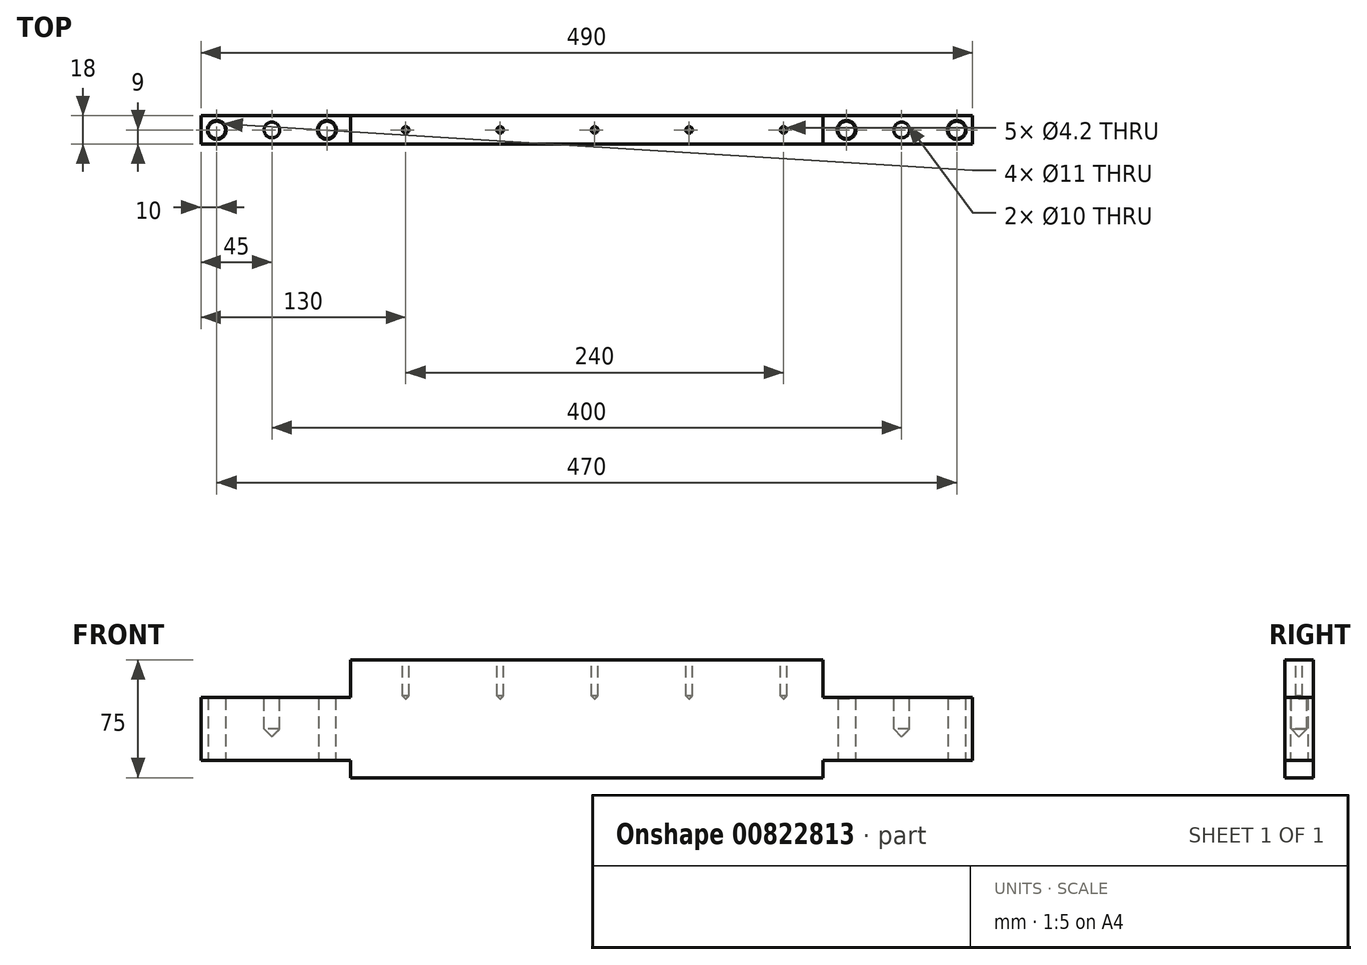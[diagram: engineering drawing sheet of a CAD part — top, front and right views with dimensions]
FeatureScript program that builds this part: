
annotation { "Feature Type Name" : "Feature", "Feature Type Description" : "" }
export const myFeature = defineFeature(function(context is Context, id is Id, definition is map)
    precondition{}
    {
        {
            var Q0;
            Q0=qCreatedBy(makeId("Front.planeOp"),FACE);
            var sketch = newSketch(context, id + "F0", { "sketchPlane" : qUnion([Q0])});
            skLineSegment(sketch, "E0.bottom", {"start": v(-245, -37.5) * mm, "end": v(245, -37.5) * mm});
            skLineSegment(sketch, "E0.top", {"start": v(-150, 37.5) * mm, "end": v(150, 37.5) * mm});
            skLineSegment(sketch, "E0.left", {"start": v(-245, -37.5) * mm, "end": v(-245, 13.5) * mm});
            skLineSegment(sketch, "E0.right", {"start": v(245, -37.5) * mm, "end": v(245, 13.5) * mm});
            skPoint(sketch, "E0.middle", {"position": v(0, 0) * mm});
            skLineSegment(sketch, "E1", {"start": v(-245, 13.5) * mm, "end": v(-150, 13.5) * mm});
            skLineSegment(sketch, "E2", {"start": v(-150, 13.5) * mm, "end": v(-150, 37.5) * mm});
            skLineSegment(sketch, "E3", {"start": v(0, 0) * mm, "end": v(0, 109.73) * mm, "construction": true});
            skPoint(sketch, "E3.endSnap0", {"position": v(0, 37.5) * mm});
            skLineSegment(sketch, "E4.MirrorCS", {"start": v(245, 13.5) * mm, "end": v(150, 13.5) * mm});
            skLineSegment(sketch, "E5.MirrorCS", {"start": v(150, 13.5) * mm, "end": v(150, 37.5) * mm});
            skPoint(sketch, "E6.orphan", {"position": v(-245, 37.5) * mm});
            skPoint(sketch, "E7.orphan", {"position": v(245, 37.5) * mm});
            skSolve(sketch);
        }
        {
            var Q0;
            Q0=qSketchRegion(id+"F0",true);
            extrude(context, id + "F1", {"entities" : qUnion([Q0]), "endBound" : BoundingType.SYMMETRIC, "depth" : 18 * mm, "offsetDistance" : 25 * mm});
        }
        {
            var Q0;
            Q0=makeQuery(id+"F1.opExtrude","SWEPT_FACE",FACE,{"disambiguationData":[OSD([sQuery(id+"F0.wireOp",EDGE,"E0.bottom")])]});
            var sketch = newSketch(context, id + "F2", { "sketchPlane" : qUnion([Q0])});
            skLineSegment(sketch, "E8", {"start": v(0, 0) * mm, "end": v(0, 32.03) * mm, "construction": true});
            skLineSegment(sketch, "E9", {"start": v(0, 32.03) * mm, "end": v(235, 0) * mm, "construction": true});
            skLineSegment(sketch, "E10", {"start": v(235, 0) * mm, "end": v(0, 0) * mm, "construction": true});
            skCircle(sketch, "E11", {"center": v(235, 0) * mm, "radius": 5.5 * mm});
            skCircle(sketch, "E12", {"center": v(165, 0) * mm, "radius": 5.5 * mm});
            skCircle(sketch, "E13.MirrorC", {"center": v(-165, 0) * mm, "radius": 5.5 * mm});
            skCircle(sketch, "E14.MirrorC", {"center": v(-235, 0) * mm, "radius": 5.5 * mm});
            skSolve(sketch);
        }
        {
            var Q0;
            Q0=qSketchRegion(id+"F2",true);
            extrude(context, id + "F3", {"entities" : qUnion([Q0]), "operationType" : NewBodyOperationType.REMOVE, "endBound" : BoundingType.UP_TO_NEXT, "oppositeDirection" : true, "depth" : 25 * mm, "offsetDistance" : 25 * mm});
        }
        {
            var Q0;
            Q0=makeQuery(id+"F1.opExtrude","SWEPT_FACE",FACE,{"disambiguationData":[OSD([sQuery(id+"F0.wireOp",EDGE,"E0.top")])]});
            var sketch = newSketch(context, id + "F4", { "sketchPlane" : qUnion([Q0])});
            skLineSegment(sketch, "E15", {"start": v(0, 0) * mm, "end": v(-175, 0) * mm, "construction": true});
            skLineSegment(sketch, "E16.0", {"start": v(-150, -9) * mm, "end": v(-150, 9) * mm, "construction": true});
            skCircle(sketch, "E17", {"center": v(-175, 0) * mm, "radius": 2.1 * mm, "construction": true});
            skLineSegment(sketch, "E18", {"start": v(-175, 0) * mm, "end": v(-195, 0) * mm, "construction": true});
            skCircle(sketch, "E19.1.0.0", {"center": v(-115, 0) * mm, "radius": 2.1 * mm});
            skCircle(sketch, "E19.2.0.0", {"center": v(-55, 0) * mm, "radius": 2.1 * mm});
            skCircle(sketch, "E19.3.0.0", {"center": v(5, 0) * mm, "radius": 2.1 * mm});
            skCircle(sketch, "E19.4.0.0", {"center": v(65, 0) * mm, "radius": 2.1 * mm});
            skCircle(sketch, "E19.5.0.0", {"center": v(125, 0) * mm, "radius": 2.1 * mm});
            skCircle(sketch, "E19.6.0.0", {"center": v(185, 0) * mm, "radius": 2.1 * mm, "construction": true});
            skCircle(sketch, "E19.7.0.0", {"center": v(245, 0) * mm, "radius": 2.1 * mm, "construction": true});
            skCircle(sketch, "E19.8.0.0", {"center": v(305, 0) * mm, "radius": 2.1 * mm, "construction": true});
            skLineSegment(sketch, "E19.direction1", {"start": v(-175, 0) * mm, "end": v(-115, 0) * mm, "construction": true});
            skLineSegment(sketch, "E20", {"start": v(0, 0) * mm, "end": v(0, 52.01) * mm, "construction": true});
            skLineSegment(sketch, "E21", {"start": v(0, 52.01) * mm, "end": v(-62, 56.3) * mm, "construction": true});
            skLineSegment(sketch, "E22", {"start": v(-62, 56.3) * mm, "end": v(-62, -65.3) * mm, "construction": true});
            skLineSegment(sketch, "E23.bottom", {"start": v(-24.5, 38.85) * mm, "end": v(-99.5, 38.85) * mm});
            skLineSegment(sketch, "E23.top", {"start": v(-24.5, -169.44) * mm, "end": v(-99.5, -169.44) * mm, "construction": true});
            skLineSegment(sketch, "E23.left", {"start": v(-24.5, 38.85) * mm, "end": v(-24.5, -169.44) * mm, "construction": true});
            skLineSegment(sketch, "E23.right", {"start": v(-99.5, 38.85) * mm, "end": v(-99.5, -169.44) * mm, "construction": true});
            skPoint(sketch, "E23.middle", {"position": v(-62, -65.3) * mm});
            skLineSegment(sketch, "E24.bottom", {"start": v(-112.5, 84.27) * mm, "end": v(-187.5, 84.27) * mm, "construction": true});
            skLineSegment(sketch, "E24.top", {"start": v(-112.5, -270.84) * mm, "end": v(-187.5, -270.84) * mm, "construction": true});
            skLineSegment(sketch, "E24.left", {"start": v(-112.5, 84.27) * mm, "end": v(-112.5, -270.84) * mm, "construction": true});
            skLineSegment(sketch, "E24.right", {"start": v(-187.5, 84.27) * mm, "end": v(-187.5, -270.84) * mm, "construction": true});
            skPoint(sketch, "E24.middle", {"position": v(-150, -93.28) * mm});
            skLineSegment(sketch, "E25", {"start": v(-150, -93.28) * mm, "end": v(0, -93.28) * mm, "construction": true});
            skLineSegment(sketch, "E26", {"start": v(0, -93.28) * mm, "end": v(0, 0) * mm, "construction": true});
            skSolve(sketch);
        }
        {
            var Q0;
            Q0=qSketchRegion(id+"F4",true);
            extrude(context, id + "F5", {"entities" : qUnion([Q0]), "operationType" : NewBodyOperationType.REMOVE, "oppositeDirection" : true, "depth" : 25 * mm, "offsetDistance" : 25 * mm});
        }
        {
            var Q0;
            Q0=makeQuery(id+"F1.opExtrude","SWEPT_FACE",FACE,{"disambiguationData":[OSD([sQuery(id+"F0.wireOp",EDGE,"E1")])]});
            var sketch = newSketch(context, id + "F6", { "sketchPlane" : qUnion([Q0])});
            skLineSegment(sketch, "E27", {"start": v(0, 0) * mm, "end": v(-200, 0) * mm, "construction": true});
            skCircle(sketch, "E28", {"center": v(-200, 0) * mm, "radius": 5 * mm});
            skCircle(sketch, "E29.0", {"center": v(-165, 0) * mm, "radius": 5.5 * mm, "construction": true});
            skCircle(sketch, "E30.0", {"center": v(-235, 0) * mm, "radius": 5.5 * mm, "construction": true});
            skLineSegment(sketch, "E31", {"start": v(0, 0) * mm, "end": v(0, -60.15) * mm, "construction": true});
            skCircle(sketch, "E32.MirrorC", {"center": v(200, 0) * mm, "radius": 5 * mm});
            skSolve(sketch);
        }
        {
            var Q0;
            Q0=qSketchRegion(id+"F6",true);
            extrude(context, id + "F7", {"entities" : qUnion([Q0]), "operationType" : NewBodyOperationType.REMOVE, "oppositeDirection" : true, "depth" : 25 * mm, "offsetDistance" : 25 * mm});
        }
        {
            var Q0;
            Q0=makeQuery(id+"F1.opExtrude","CAP_FACE",FACE,{"disambiguationData":[OSD([sQuery(id+"F0.wireOp",EDGE,"E0.bottom"),sQuery(id+"F0.wireOp",EDGE,"E0.top"),sQuery(id+"F0.wireOp",EDGE,"E0.left"),sQuery(id+"F0.wireOp",EDGE,"E0.right"),sQuery(id+"F0.wireOp",EDGE,"E1"),sQuery(id+"F0.wireOp",EDGE,"E2"),sQuery(id+"F0.wireOp",EDGE,"E4.MirrorCS"),sQuery(id+"F0.wireOp",EDGE,"E5.MirrorCS")])],"isStart":false});
            var sketch = newSketch(context, id + "F8", { "sketchPlane" : qUnion([Q0])});
            skLineSegment(sketch, "E33.0.0", {"start": v(150, 37.5) * mm, "end": v(-150, 37.5) * mm, "construction": true});
            skLineSegment(sketch, "E33.0.1", {"start": v(-150, 37.5) * mm, "end": v(-150, 13.5) * mm, "construction": true});
            skLineSegment(sketch, "E33.0.2", {"start": v(-150, 13.5) * mm, "end": v(-245, 13.5) * mm, "construction": true});
            skLineSegment(sketch, "E33.0.3", {"start": v(-245, 13.5) * mm, "end": v(-245, -37.5) * mm, "construction": true});
            skLineSegment(sketch, "E33.0.4", {"start": v(-245, -37.5) * mm, "end": v(245, -37.5) * mm, "construction": true});
            skLineSegment(sketch, "E33.0.5", {"start": v(245, -37.5) * mm, "end": v(245, 13.5) * mm, "construction": true});
            skLineSegment(sketch, "E33.0.6", {"start": v(245, 13.5) * mm, "end": v(150, 13.5) * mm, "construction": true});
            skLineSegment(sketch, "E33.0.7", {"start": v(150, 13.5) * mm, "end": v(150, 37.5) * mm, "construction": true});
            skLineSegment(sketch, "E34", {"start": v(0, 0) * mm, "end": v(0, -112.2) * mm, "construction": true});
            skLineSegment(sketch, "E35.bottom", {"start": v(-245, -37.5) * mm, "end": v(-150, -37.5) * mm});
            skLineSegment(sketch, "E35.top", {"start": v(-245, -26.5) * mm, "end": v(-150, -26.5) * mm});
            skLineSegment(sketch, "E35.left", {"start": v(-245, -37.5) * mm, "end": v(-245, -26.5) * mm});
            skLineSegment(sketch, "E35.right", {"start": v(-150, -37.5) * mm, "end": v(-150, -26.5) * mm});
            skLineSegment(sketch, "E36.MirrorCS", {"start": v(245, -26.5) * mm, "end": v(150, -26.5) * mm});
            skLineSegment(sketch, "E37.MirrorCS", {"start": v(245, -37.5) * mm, "end": v(150, -37.5) * mm});
            skLineSegment(sketch, "E38.MirrorCS", {"start": v(150, -37.5) * mm, "end": v(150, -26.5) * mm});
            skLineSegment(sketch, "E39.MirrorCS", {"start": v(245, -37.5) * mm, "end": v(245, -26.5) * mm});
            skSolve(sketch);
        }
        {
            var Q0;
            Q0 = qSketchRegion(id + "F8", true);
            extrude(context, id + "F9", {"entities" : qUnion([Q0]), "operationType" : NewBodyOperationType.REMOVE, "oppositeDirection" : true, "depth" : 25 * mm, "offsetDistance" : 25 * mm});
        }
        {
            var Q0;
            Q0=makeQuery(id+"F7.boolean.opBoolean","COPY",FACE,{"derivedFrom":makeQuery(id+"F7.opExtrude","CAP_FACE",FACE,{"disambiguationData":[OSD([sQuery(id+"F6.wireOp",EDGE,"E28")])],"isStart":false})});
            var Q1;
            Q1=makeQuery(id+"F7.boolean.opBoolean","COPY",FACE,{"derivedFrom":makeQuery(id+"F7.opExtrude","CAP_FACE",FACE,{"disambiguationData":[OSD([sQuery(id+"F6.wireOp",EDGE,"E32.MirrorC")])],"isStart":false})});
            chamfer(context, id + "F10", {"entities" : qUnion([Q0, Q1]), "width" : 5 * mm, "tangentPropagation" : true});
        }
        {
            var Q0;
            Q0=makeQuery(id+"F5.boolean.opBoolean","COPY",FACE,{"derivedFrom":makeQuery(id+"F5.opExtrude","CAP_FACE",FACE,{"disambiguationData":[OSD([sQuery(id+"F4.wireOp",EDGE,"E19.5.0.0")])],"isStart":false})});
            var Q1;
            Q1=makeQuery(id+"F5.boolean.opBoolean","COPY",FACE,{"derivedFrom":makeQuery(id+"F5.opExtrude","CAP_FACE",FACE,{"disambiguationData":[OSD([sQuery(id+"F4.wireOp",EDGE,"E19.4.0.0")])],"isStart":false})});
            var Q2;
            Q2=makeQuery(id+"F5.boolean.opBoolean","COPY",FACE,{"derivedFrom":makeQuery(id+"F5.opExtrude","CAP_FACE",FACE,{"disambiguationData":[OSD([sQuery(id+"F4.wireOp",EDGE,"E19.3.0.0")])],"isStart":false})});
            var Q3;
            Q3=makeQuery(id+"F5.boolean.opBoolean","COPY",FACE,{"derivedFrom":makeQuery(id+"F5.opExtrude","CAP_FACE",FACE,{"disambiguationData":[OSD([sQuery(id+"F4.wireOp",EDGE,"E19.2.0.0")])],"isStart":false})});
            var Q4;
            Q4=makeQuery(id+"F5.boolean.opBoolean","COPY",FACE,{"derivedFrom":makeQuery(id+"F5.opExtrude","CAP_FACE",FACE,{"disambiguationData":[OSD([sQuery(id+"F4.wireOp",EDGE,"E19.1.0.0")])],"isStart":false})});
            chamfer(context, id + "F11", {"entities" : qUnion([Q0, Q1, Q2, Q3, Q4]), "width" : 2.1 * mm, "tangentPropagation" : true});
        }
        {
            var Q0;
            Q0=makeQuery(id+"F3.boolean.opBoolean","COPY",FACE,{"derivedFrom":makeQuery(id+"F3.opExtrude","SWEPT_FACE",FACE,{"disambiguationData":[OSD([sQuery(id+"F2.wireOp",EDGE,"E13.MirrorC")])]})});
            var Q1;
            Q1=makeQuery(id+"F3.boolean.opBoolean","COPY",FACE,{"derivedFrom":makeQuery(id+"F3.opExtrude","SWEPT_FACE",FACE,{"disambiguationData":[OSD([sQuery(id+"F2.wireOp",EDGE,"E14.MirrorC")])]})});
            var Q2;
            Q2=makeQuery(id+"F7.boolean.opBoolean","COPY",EDGE,{"derivedFrom":makeQuery(id+"F7.opExtrude","CAP_EDGE",EDGE,{"disambiguationData":[OSD([sQuery(id+"F6.wireOp",EDGE,"E28")])],"isStart":true})});
            var Q3;
            Q3=makeQuery(id+"F5.boolean.opBoolean","COPY",EDGE,{"derivedFrom":makeQuery(id+"F5.opExtrude","CAP_EDGE",EDGE,{"disambiguationData":[OSD([sQuery(id+"F4.wireOp",EDGE,"E19.1.0.0")])],"isStart":true})});
            var Q4;
            Q4=makeQuery(id+"F5.boolean.opBoolean","COPY",EDGE,{"derivedFrom":makeQuery(id+"F5.opExtrude","CAP_EDGE",EDGE,{"disambiguationData":[OSD([sQuery(id+"F4.wireOp",EDGE,"E19.2.0.0")])],"isStart":true})});
            var Q5;
            Q5=makeQuery(id+"F5.boolean.opBoolean","COPY",EDGE,{"derivedFrom":makeQuery(id+"F5.opExtrude","CAP_EDGE",EDGE,{"disambiguationData":[OSD([sQuery(id+"F4.wireOp",EDGE,"E19.3.0.0")])],"isStart":true})});
            var Q6;
            Q6=makeQuery(id+"F5.boolean.opBoolean","COPY",EDGE,{"derivedFrom":makeQuery(id+"F5.opExtrude","CAP_EDGE",EDGE,{"disambiguationData":[OSD([sQuery(id+"F4.wireOp",EDGE,"E19.4.0.0")])],"isStart":true})});
            var Q7;
            Q7=makeQuery(id+"F5.boolean.opBoolean","COPY",EDGE,{"derivedFrom":makeQuery(id+"F5.opExtrude","CAP_EDGE",EDGE,{"disambiguationData":[OSD([sQuery(id+"F4.wireOp",EDGE,"E19.5.0.0")])],"isStart":true})});
            var Q8;
            Q8=makeQuery(id+"F3.boolean.opBoolean","COPY",FACE,{"derivedFrom":makeQuery(id+"F3.opExtrude","SWEPT_FACE",FACE,{"disambiguationData":[OSD([sQuery(id+"F2.wireOp",EDGE,"E12")])]})});
            var Q9;
            Q9=makeQuery(id+"F3.boolean.opBoolean","COPY",FACE,{"derivedFrom":makeQuery(id+"F3.opExtrude","SWEPT_FACE",FACE,{"disambiguationData":[OSD([sQuery(id+"F2.wireOp",EDGE,"E11")])]})});
            var Q10;
            Q10=makeQuery(id+"F7.boolean.opBoolean","COPY",EDGE,{"derivedFrom":makeQuery(id+"F7.opExtrude","CAP_EDGE",EDGE,{"disambiguationData":[OSD([sQuery(id+"F6.wireOp",EDGE,"E32.MirrorC")])],"isStart":true})});
            chamfer(context, id + "F12", {"entities" : qUnion([Q0, Q1, Q2, Q3, Q4, Q5, Q6, Q7, Q8, Q9, Q10]), "width" : 0.5 * mm, "tangentPropagation" : true});
        }
    });
